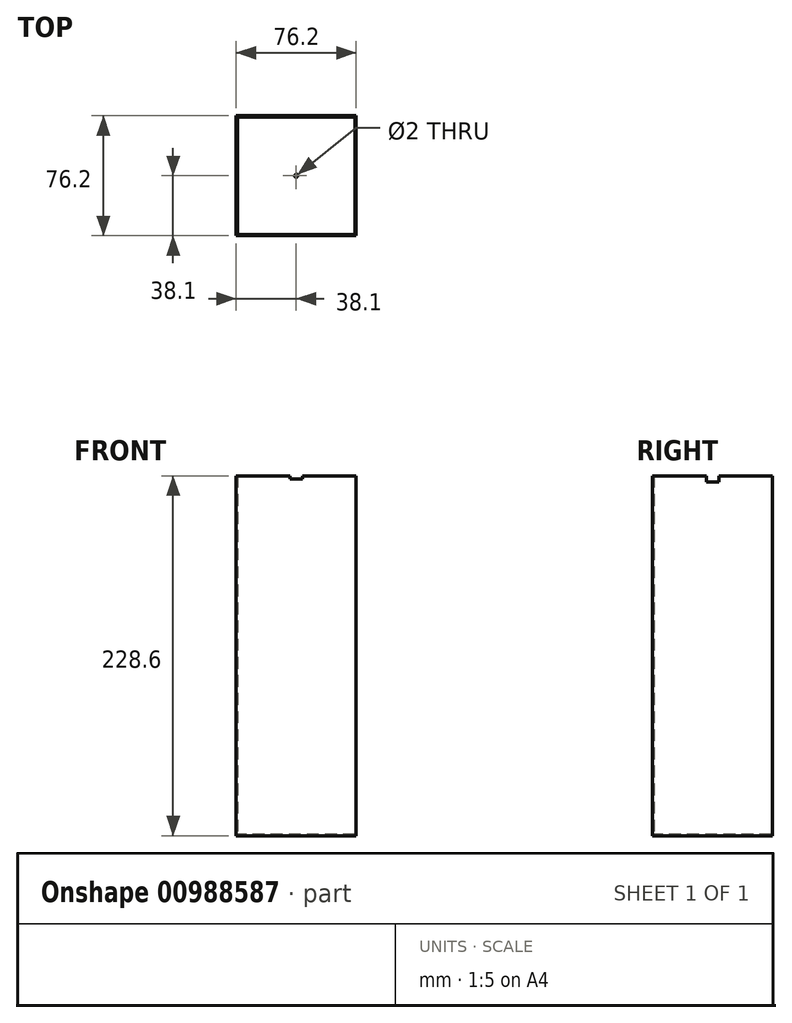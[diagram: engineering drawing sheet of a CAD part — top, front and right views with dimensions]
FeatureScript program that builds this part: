
annotation { "Feature Type Name" : "Feature", "Feature Type Description" : "" }
export const myFeature = defineFeature(function(context is Context, id is Id, definition is map)
    precondition{}
    {
        {
            var Q0;
            Q0=qCreatedBy(makeId("Top.planeOp"),FACE);
            var sketch = newSketch(context, id + "F0", { "sketchPlane" : qUnion([Q0])});
            skLineSegment(sketch, "E0.bottom", {"start": v(38.1, 38.1) * mm, "end": v(-38.1, 38.1) * mm});
            skLineSegment(sketch, "E0.top", {"start": v(38.1, -38.1) * mm, "end": v(-38.1, -38.1) * mm});
            skLineSegment(sketch, "E0.left", {"start": v(38.1, 38.1) * mm, "end": v(38.1, -38.1) * mm});
            skLineSegment(sketch, "E0.right", {"start": v(-38.1, 38.1) * mm, "end": v(-38.1, -38.1) * mm});
            skPoint(sketch, "E0.middle", {"position": v(0, 0) * mm});
            skSolve(sketch);
        }
        {
            var Q0;
            Q0=qSketchRegion(id+"F0",true);
            extrude(context, id + "F1", {"entities" : qUnion([Q0]), "depth" : 228.6 * mm, "offsetDistance" : 25.4 * mm});
        }
        {
            var Q0;
            Q0=makeQuery(id+"F1.opExtrude","CAP_FACE",FACE,{"disambiguationData":[OSD([sQuery(id+"F0.wireOp",EDGE,"E0.bottom"),sQuery(id+"F0.wireOp",EDGE,"E0.top"),sQuery(id+"F0.wireOp",EDGE,"E0.left"),sQuery(id+"F0.wireOp",EDGE,"E0.right")])],"isStart":false});
            shell(context, id + "F2", {"entities" : qUnion([Q0]), "thickness" : 0.8 * mm});
        }
        {
            var Q0;
            Q0=makeQuery(id+"F2.opShell","OFFSET_FACE",FACE,{"disambiguationData":[OSD([sQuery(id+"F0.wireOp",EDGE,"E0.bottom"),sQuery(id+"F0.wireOp",EDGE,"E0.top"),sQuery(id+"F0.wireOp",EDGE,"E0.left"),sQuery(id+"F0.wireOp",EDGE,"E0.right")])]});
            var sketch = newSketch(context, id + "F3", { "sketchPlane" : qUnion([Q0])});
            skCircle(sketch, "E1", {"center": v(0, 0) * mm, "radius": 1 * mm});
            skSolve(sketch);
        }
        {
            var Q0;
            Q0=qSketchRegion(id+"F3",true);
            extrude(context, id + "F4", {"entities" : qUnion([Q0]), "operationType" : NewBodyOperationType.REMOVE, "oppositeDirection" : true, "depth" : 25.4 * mm, "offsetDistance" : 25.4 * mm});
        }
        {
            var Q0;
            Q0=makeQuery(id+"F1.opExtrude","SWEPT_FACE",FACE,{"disambiguationData":[OSD([sQuery(id+"F0.wireOp",EDGE,"E0.top")])]});
            var sketch = newSketch(context, id + "F5", { "sketchPlane" : qUnion([Q0])});
            skLineSegment(sketch, "E2", {"start": v(-4, 228.6) * mm, "end": v(4, 228.6) * mm});
            skLineSegment(sketch, "E3", {"start": v(-4, 228.6) * mm, "end": v(-4, 226.6) * mm});
            skLineSegment(sketch, "E4", {"start": v(4, 228.6) * mm, "end": v(4, 226.6) * mm});
            skLineSegment(sketch, "E5", {"start": v(4, 226.6) * mm, "end": v(-4, 226.6) * mm});
            skSolve(sketch);
        }
        {
            var Q0;
            Q0=qSketchRegion(id+"F5",true);
            extrude(context, id + "F6", {"entities" : qUnion([Q0]), "operationType" : NewBodyOperationType.REMOVE, "endBound" : BoundingType.THROUGH_ALL, "oppositeDirection" : true, "depth" : 25.4 * mm, "offsetDistance" : 25.4 * mm});
        }
        {
            var Q0;
            Q0=makeQuery(id+"F1.opExtrude","SWEPT_FACE",FACE,{"disambiguationData":[OSD([sQuery(id+"F0.wireOp",EDGE,"E0.left")])]});
            var sketch = newSketch(context, id + "F7", { "sketchPlane" : qUnion([Q0])});
            skLineSegment(sketch, "E6", {"start": v(-4, 228.6) * mm, "end": v(4, 228.6) * mm});
            skLineSegment(sketch, "E7", {"start": v(-4, 228.6) * mm, "end": v(-4, 224.6) * mm});
            skLineSegment(sketch, "E8", {"start": v(4, 228.6) * mm, "end": v(4, 224.6) * mm});
            skLineSegment(sketch, "E9", {"start": v(4, 224.6) * mm, "end": v(-4, 224.6) * mm});
            skSolve(sketch);
        }
        {
            var Q0;
            Q0=qSketchRegion(id+"F7",true);
            extrude(context, id + "F8", {"entities" : qUnion([Q0]), "operationType" : NewBodyOperationType.REMOVE, "endBound" : BoundingType.THROUGH_ALL, "oppositeDirection" : true, "depth" : 25.4 * mm, "offsetDistance" : 25.4 * mm});
        }
    });
